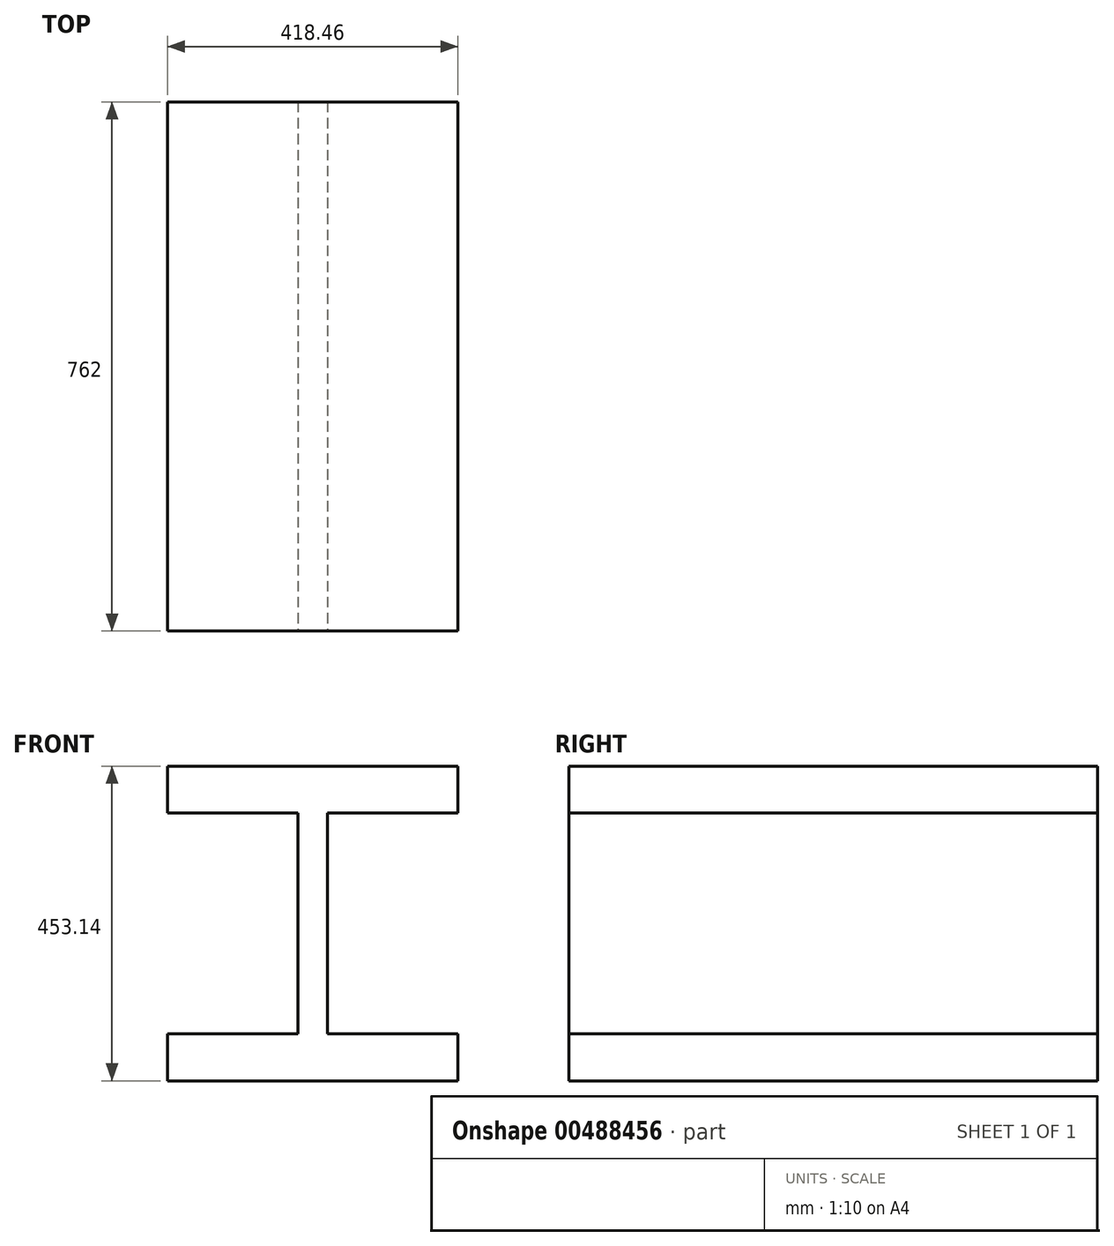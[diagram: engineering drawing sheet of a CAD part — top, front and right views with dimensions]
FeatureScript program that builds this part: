
annotation { "Feature Type Name" : "Feature", "Feature Type Description" : "" }
export const myFeature = defineFeature(function(context is Context, id is Id, definition is map)
    precondition{}
    {
        {
            var Q0;
            Q0=qCreatedBy(makeId("Front.planeOp"),FACE);
            var sketch = newSketch(context, id + "F0", { "sketchPlane" : qUnion([Q0])});
            skLineSegment(sketch, "E0", {"start": v(0, 0) * mm, "end": v(0, 226.57) * mm});
            skLineSegment(sketch, "E1", {"start": v(0, 226.57) * mm, "end": v(-209.23, 226.57) * mm});
            skLineSegment(sketch, "E2", {"start": v(-209.23, 226.57) * mm, "end": v(-209.23, 159) * mm});
            skLineSegment(sketch, "E3", {"start": v(-209.23, 159) * mm, "end": v(-21.02, 159) * mm});
            skLineSegment(sketch, "E4", {"start": v(-21.02, 159) * mm, "end": v(-21.02, 0) * mm});
            skLineSegment(sketch, "E5", {"start": v(-21.02, 0) * mm, "end": v(0, 0) * mm});
            skSolve(sketch);
        }
        {
            var Q0;
            Q0=makeQuery(id+"F0.imprint","IMPRINT",FACE,{"disambiguationData":[TD([[makeQuery(id+"F0.imprint","IMPRINT",EDGE,{"derivedFrom":sQuery(id+"F0.wireOp",EDGE,"E0")}),1.0]])]});
            extrude(context, id + "F1", {"entities" : qUnion([Q0]), "oppositeDirection" : true, "depth" : 762 * mm});
        }
        {
            var Q0;
            Q0=makeQuery(id+"F1.opExtrude","SWEPT_BODY",BODY,{"disambiguationData":[OSD([sQuery(id+"F0.wireOp",EDGE,"E0"),sQuery(id+"F0.wireOp",EDGE,"E1"),sQuery(id+"F0.wireOp",EDGE,"E2"),sQuery(id+"F0.wireOp",EDGE,"E3"),sQuery(id+"F0.wireOp",EDGE,"E4"),sQuery(id+"F0.wireOp",EDGE,"E5")])]});
            var Q1;
            Q1=qCreatedBy(makeId("Top.planeOp"),FACE);
            mirror(context, id + "F2", {"operationType" : NewBodyOperationType.ADD, "entities" : qUnion([Q0]), "mirrorPlane" : qUnion([Q1])});
        }
        {
            var Q0;
            Q0=makeQuery(id+"F1.opExtrude","SWEPT_BODY",BODY,{"disambiguationData":[OSD([sQuery(id+"F0.wireOp",EDGE,"E0"),sQuery(id+"F0.wireOp",EDGE,"E1"),sQuery(id+"F0.wireOp",EDGE,"E2"),sQuery(id+"F0.wireOp",EDGE,"E3"),sQuery(id+"F0.wireOp",EDGE,"E4"),sQuery(id+"F0.wireOp",EDGE,"E5")])]});
            var Q1;
            Q1=qCreatedBy(makeId("Right.planeOp"),FACE);
            mirror(context, id + "F3", {"operationType" : NewBodyOperationType.ADD, "entities" : qUnion([Q0]), "mirrorPlane" : qUnion([Q1])});
        }
    });
